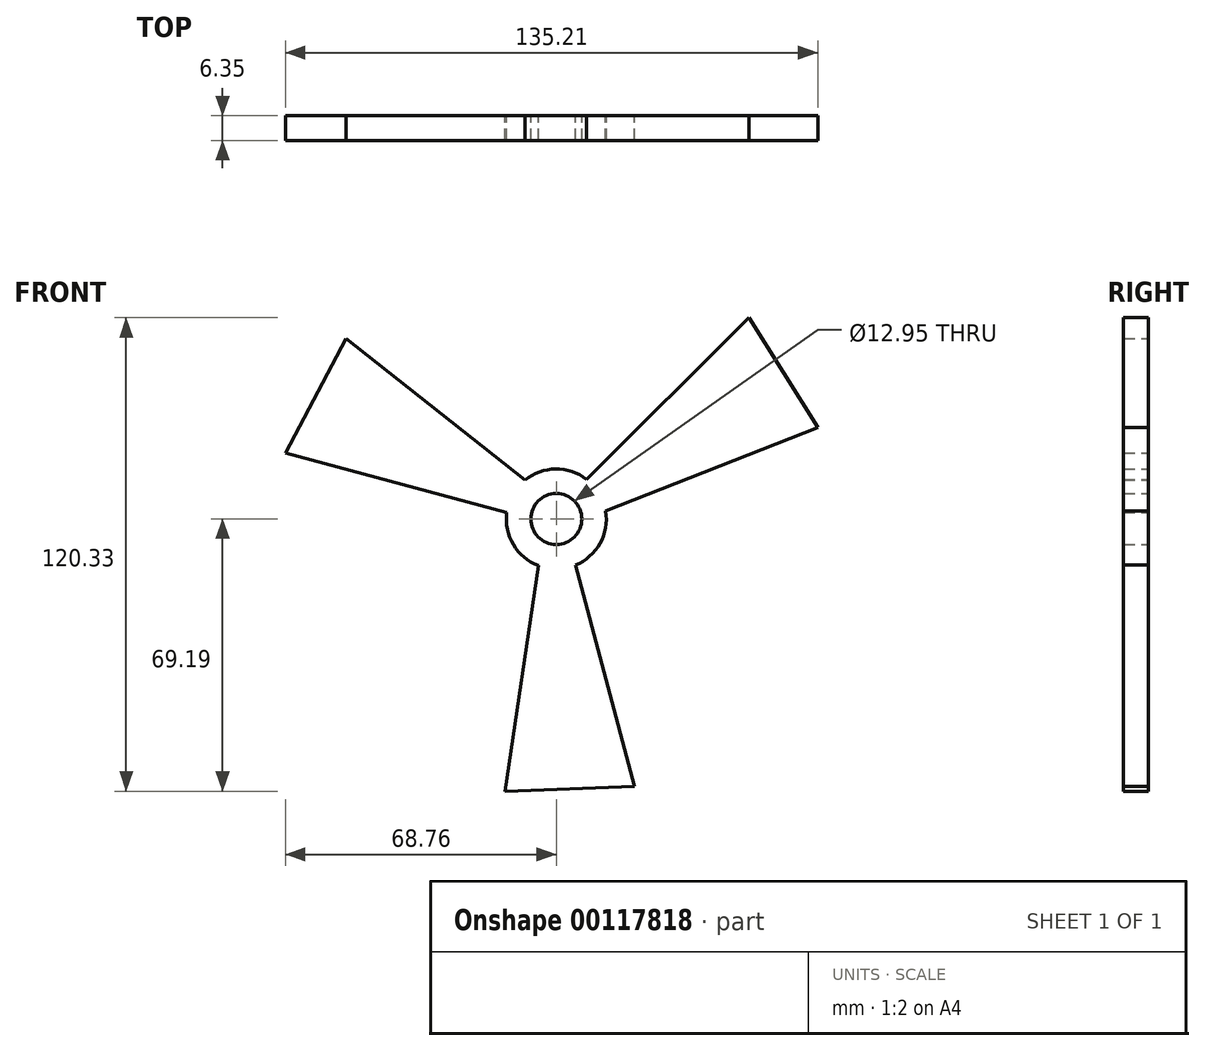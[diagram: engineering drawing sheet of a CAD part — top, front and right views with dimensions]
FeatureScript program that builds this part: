
annotation { "Feature Type Name" : "Feature", "Feature Type Description" : "" }
export const myFeature = defineFeature(function(context is Context, id is Id, definition is map)
    precondition{}
    {
        {
            var Q0;
            Q0=qCreatedBy(makeId("Front.planeOp"),FACE);
            var sketch = newSketch(context, id + "F0", { "sketchPlane" : qUnion([Q0])});
            skCircle(sketch, "E0", {"center": v(0, 0) * mm, "radius": 6.48 * mm});
            skCircle(sketch, "E1", {"center": v(0, 0) * mm, "radius": 12.7 * mm});
            skLineSegment(sketch, "E2", {"start": v(-8, 9.87) * mm, "end": v(-53.39, 45.91) * mm});
            skLineSegment(sketch, "E3", {"start": v(-53.39, 45.91) * mm, "end": v(-68.76, 16.81) * mm});
            skLineSegment(sketch, "E4", {"start": v(-68.76, 16.81) * mm, "end": v(-12.6, 1.65) * mm});
            skLineSegment(sketch, "E5.1.0", {"start": v(19.82, -67.95) * mm, "end": v(4.87, -11.73) * mm});
            skLineSegment(sketch, "E5.1.1", {"start": v(-13.07, -69.2) * mm, "end": v(19.82, -67.95) * mm});
            skLineSegment(sketch, "E5.1.2", {"start": v(-4.55, -11.86) * mm, "end": v(-13.07, -69.2) * mm});
            skLineSegment(sketch, "E5.2.0", {"start": v(48.94, 51.14) * mm, "end": v(7.73, 10.08) * mm});
            skLineSegment(sketch, "E5.2.1", {"start": v(66.45, 23.28) * mm, "end": v(48.94, 51.14) * mm});
            skLineSegment(sketch, "E5.2.2", {"start": v(12.54, 1.99) * mm, "end": v(66.45, 23.28) * mm});
            skPoint(sketch, "E6.orphan", {"position": v(-6.48, 0) * mm});
            skPoint(sketch, "E7.orphan", {"position": v(-2.88, 5.8) * mm});
            skPoint(sketch, "E8.orphan", {"position": v(3.24, 5.6) * mm});
            skPoint(sketch, "E9.orphan", {"position": v(6.46, -0.41) * mm});
            skPoint(sketch, "E10.orphan", {"position": v(3.24, -5.6) * mm});
            skPoint(sketch, "E11.orphan", {"position": v(-3.59, -5.4) * mm});
            skSolve(sketch);
        }
        {
            var Q0;
            Q0 = qSketchRegion(id + "F0", true);
            extrude(context, id + "F1", {"entities" : qUnion([Q0]), "depth" : 6.35 * mm});
        }
    });
